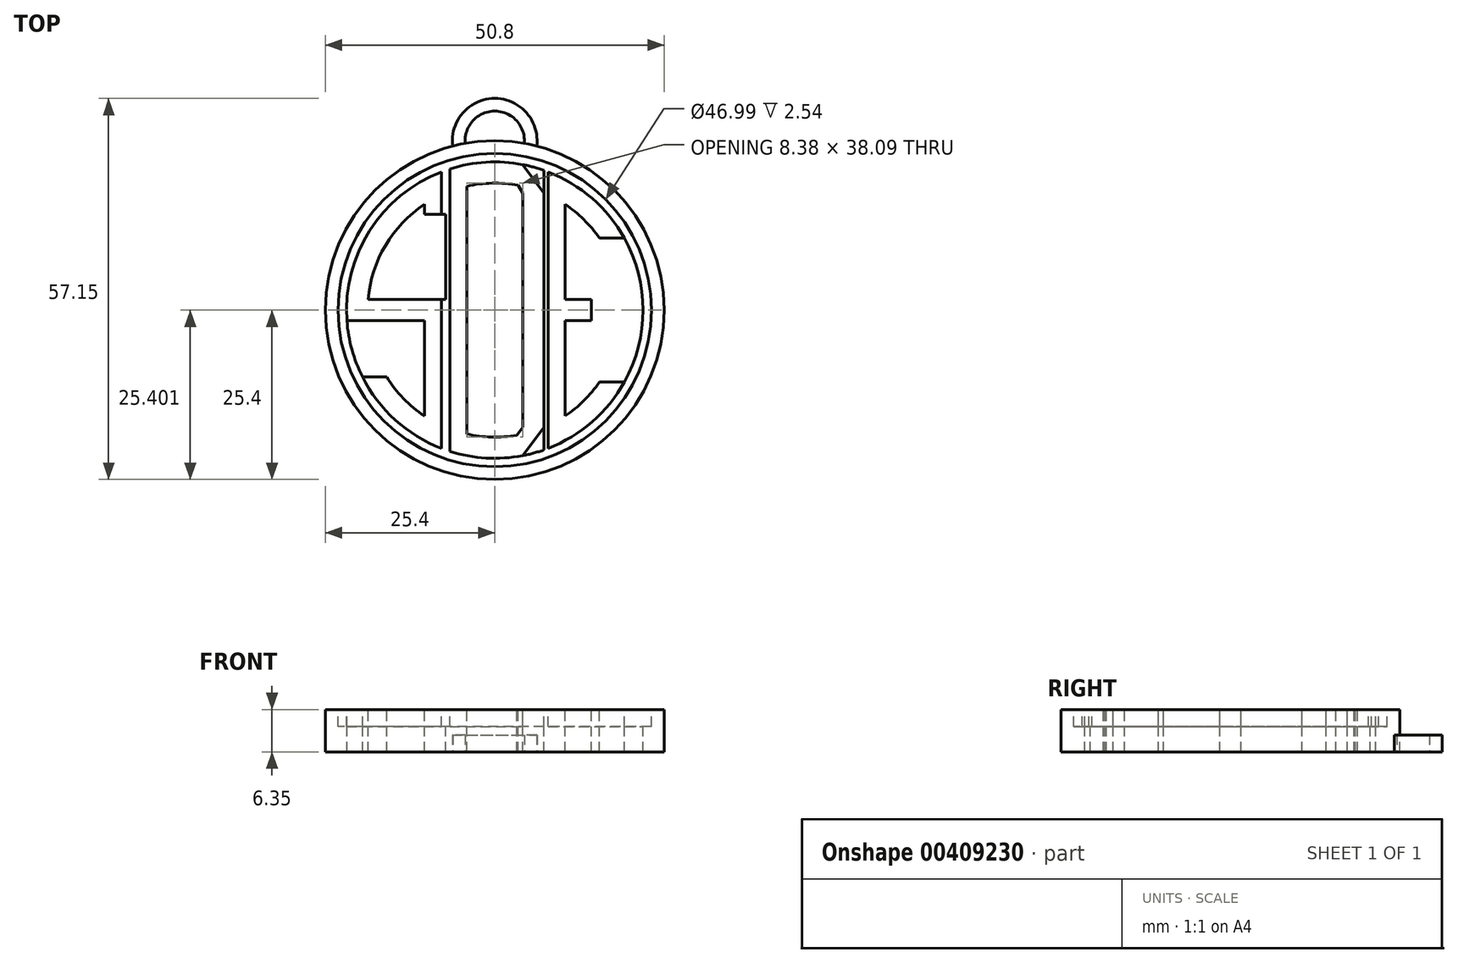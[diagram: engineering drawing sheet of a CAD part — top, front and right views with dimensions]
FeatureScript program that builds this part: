
annotation { "Feature Type Name" : "Feature", "Feature Type Description" : "" }
export const myFeature = defineFeature(function(context is Context, id is Id, definition is map)
    precondition{}
    {
        {
            var Q0;
            Q0=qCreatedBy(makeId("Top.planeOp"),FACE);
            var sketch = newSketch(context, id + "F0", { "sketchPlane" : qUnion([Q0])});
            skCircle(sketch, "E0", {"center": v(0, 0) * mm, "radius": 25.4 * mm});
            skCircle(sketch, "E1", {"center": v(0, 0) * mm, "radius": 22.23 * mm});
            skLineSegment(sketch, "E2", {"start": v(0, 0) * mm, "end": v(7.37, 0) * mm, "construction": true});
            skLineSegment(sketch, "E3", {"start": v(0, 0) * mm, "end": v(-7.37, 0) * mm, "construction": true});
            skLineSegment(sketch, "E4", {"start": v(7.37, 17.57) * mm, "end": v(7.37, 1.59) * mm});
            skLineSegment(sketch, "E5", {"start": v(-7.37, 20.97) * mm, "end": v(-7.37, -20.97) * mm, "construction": true});
            skPoint(sketch, "E6", {"position": v(-7.37, 1.59) * mm});
            skPoint(sketch, "E7", {"position": v(-7.37, -1.59) * mm});
            skArc(sketch, "E8", {"start": v(-16.2, -10.03) * mm, "mid": v(-13.68, -13.25) * mm, "end": v(-10.54, -15.87) * mm});
            skLineSegment(sketch, "E9", {"start": v(-7.37, 1.59) * mm, "end": v(-18.98, 1.59) * mm});
            skLineSegment(sketch, "E10", {"start": v(-10.54, -1.59) * mm, "end": v(-18.98, -1.59) * mm});
            skLineSegment(sketch, "E11", {"start": v(-7.37, 17.57) * mm, "end": v(-7.37, 14.4) * mm});
            skLineSegment(sketch, "E12", {"start": v(-7.37, 14.4) * mm, "end": v(-10.54, 14.4) * mm});
            skLineSegment(sketch, "E13", {"start": v(-10.54, 14.4) * mm, "end": v(-10.54, 15.87) * mm});
            skPoint(sketch, "E14", {"position": v(-10.54, -1.59) * mm});
            skLineSegment(sketch, "E15", {"start": v(-7.37, -1.59) * mm, "end": v(-7.37, -17.57) * mm});
            skLineSegment(sketch, "E16", {"start": v(-10.54, -1.59) * mm, "end": v(-10.54, -15.87) * mm});
            skLineSegment(sketch, "E17", {"start": v(-19.83, -10.03) * mm, "end": v(-16.2, -10.03) * mm});
            skPoint(sketch, "E18", {"position": v(-4.2, 0) * mm});
            skLineSegment(sketch, "E19", {"start": v(-4.2, 18.58) * mm, "end": v(-4.2, 1.59) * mm});
            skPoint(sketch, "E20", {"position": v(10.54, 0) * mm});
            skLineSegment(sketch, "E21", {"start": v(10.54, 15.87) * mm, "end": v(10.54, 1.59) * mm});
            skLineSegment(sketch, "E22", {"start": v(-18.98, -1.59) * mm, "end": v(-22.17, -1.59) * mm});
            skArc(sketch, "E23.trimOffspring", {"start": v(-10.54, 15.87) * mm, "mid": v(-16.4, 9.7) * mm, "end": v(-18.98, 1.59) * mm});
            skArc(sketch, "E24.trimOffspring", {"start": v(3.47, 18.73) * mm, "mid": v(-0.37, 19.05) * mm, "end": v(-4.2, 18.58) * mm});
            skPoint(sketch, "E25.orphan", {"position": v(7.37, 20.97) * mm});
            skLineSegment(sketch, "E26.trimOffspring", {"start": v(-4.2, -1.59) * mm, "end": v(-4.2, -18.58) * mm});
            skLineSegment(sketch, "E27.trimOffspring", {"start": v(7.37, -1.59) * mm, "end": v(7.37, -17.57) * mm});
            skArc(sketch, "E28.trimOffspring", {"start": v(-4.2, -18.58) * mm, "mid": v(-0.45, -19.04) * mm, "end": v(3.3, -18.76) * mm});
            skArc(sketch, "E29.trimOffspring", {"start": v(10.54, -15.87) * mm, "mid": v(13.36, -13.58) * mm, "end": v(15.7, -10.79) * mm});
            skLineSegment(sketch, "E30", {"start": v(-7.37, 14.4) * mm, "end": v(-7.37, 1.59) * mm});
            skPoint(sketch, "E31", {"position": v(-8, 14.4) * mm});
            skPoint(sketch, "E32", {"position": v(-6.73, 14.4) * mm});
            skLineSegment(sketch, "E33", {"start": v(-6.73, 14.4) * mm, "end": v(-8, 14.4) * mm});
            skLineSegment(sketch, "E34", {"start": v(-8, 20.73) * mm, "end": v(-8, 14.4) * mm});
            skLineSegment(sketch, "E35", {"start": v(-6.73, 14.4) * mm, "end": v(-6.73, 21.18) * mm});
            skPoint(sketch, "E36", {"position": v(4.2, 17.57) * mm});
            skLineSegment(sketch, "E37", {"start": v(4.2, 17.57) * mm, "end": v(4.2, -17.57) * mm});
            skLineSegment(sketch, "E38", {"start": v(7.37, 17.57) * mm, "end": v(7.37, 20.97) * mm});
            skLineSegment(sketch, "E39", {"start": v(-4.2, 1.59) * mm, "end": v(-4.2, -1.59) * mm});
            skLineSegment(sketch, "E40", {"start": v(14.48, 1.59) * mm, "end": v(14.48, -1.59) * mm});
            skLineSegment(sketch, "E41", {"start": v(14.48, -1.59) * mm, "end": v(10.54, -1.59) * mm});
            skLineSegment(sketch, "E42", {"start": v(15.7, 10.79) * mm, "end": v(19.43, 10.79) * mm});
            skLineSegment(sketch, "E43", {"start": v(15.7, -10.79) * mm, "end": v(19.43, -10.79) * mm});
            skPoint(sketch, "E44", {"position": v(-8, -1.59) * mm});
            skPoint(sketch, "E45", {"position": v(-6.73, -1.59) * mm});
            skLineSegment(sketch, "E46", {"start": v(-6.73, -1.59) * mm, "end": v(-8, -1.59) * mm});
            skLineSegment(sketch, "E47", {"start": v(-8, -1.59) * mm, "end": v(-8, -20.73) * mm});
            skLineSegment(sketch, "E48", {"start": v(-6.73, -1.59) * mm, "end": v(-6.73, -21.18) * mm});
            skLineSegment(sketch, "E49", {"start": v(-8, -1.59) * mm, "end": v(-8, 1.59) * mm});
            skPoint(sketch, "E50", {"position": v(-6.73, 1.56) * mm});
            skLineSegment(sketch, "E51", {"start": v(-7.37, 1.59) * mm, "end": v(-6.73, 1.56) * mm});
            skLineSegment(sketch, "E52", {"start": v(-6.73, -1.59) * mm, "end": v(-6.73, 1.56) * mm});
            skPoint(sketch, "E53", {"position": v(8, 20.97) * mm});
            skPoint(sketch, "E54", {"position": v(7.37, -20.97) * mm});
            skPoint(sketch, "E55", {"position": v(8, -20.97) * mm});
            skLineSegment(sketch, "E56", {"start": v(7.37, -20.97) * mm, "end": v(7.37, -17.57) * mm});
            skLineSegment(sketch, "E57", {"start": v(7.37, 1.59) * mm, "end": v(7.37, -1.59) * mm});
            skLineSegment(sketch, "E58", {"start": v(7.37, 17.57) * mm, "end": v(4.2, 21.83) * mm});
            skLineSegment(sketch, "E59", {"start": v(4.2, 17.57) * mm, "end": v(3.47, 18.73) * mm});
            skPoint(sketch, "E59.endSnap0", {"position": v(5.78, 19.7) * mm});
            skPoint(sketch, "E60", {"position": v(4.2, -17.57) * mm});
            skLineSegment(sketch, "E61", {"start": v(7.37, -17.57) * mm, "end": v(4.2, -21.83) * mm});
            skLineSegment(sketch, "E62", {"start": v(4.2, -17.57) * mm, "end": v(3.3, -18.76) * mm});
            skLineSegment(sketch, "E63", {"start": v(-6.73, 14.4) * mm, "end": v(-6.73, 1.56) * mm});
            skPoint(sketch, "E64.orphan", {"position": v(2.87, 19.7) * mm});
            skPoint(sketch, "E65.start.orphan", {"position": v(4.2, 18.58) * mm});
            skPoint(sketch, "E66.orphan", {"position": v(4.2, -18.58) * mm});
            skLineSegment(sketch, "E67", {"start": v(14.48, 1.59) * mm, "end": v(10.54, 1.59) * mm});
            skLineSegment(sketch, "E68.trimOffspring", {"start": v(10.54, -1.59) * mm, "end": v(10.54, -15.87) * mm});
            skArc(sketch, "E69.trimOffspring", {"start": v(15.7, 10.79) * mm, "mid": v(13.36, 13.58) * mm, "end": v(10.54, 15.87) * mm});
            skCircle(sketch, "E70", {"center": v(0, 0) * mm, "radius": 23.5 * mm});
            skLineSegment(sketch, "E71", {"start": v(8, 20.73) * mm, "end": v(8, -20.73) * mm});
            skPoint(sketch, "E72", {"position": v(8, 20.72) * mm});
            skSolve(sketch);
        }
        {
            var Q0;
            Q0=makeQuery(id+"F0.imprint","IMPRINT",FACE,{"disambiguationData":[TD([[makeQuery(id+"F0.imprint","IMPRINT",EDGE,{"derivedFrom":sQuery(id+"F0.wireOp",EDGE,"E0")}),1.0]])]});
            var Q1;
            Q1=makeQuery(id+"F0.imprint","IMPRINT",FACE,{"disambiguationData":[TD([[makeQuery(id+"F0.imprint","IMPRINT",EDGE,{"derivedFrom":sQuery(id+"F0.wireOp",EDGE,"E8")}),-1.0]])]});
            var Q2;
            {var subQ0=sQuery(id+"F0.wireOp",EDGE,"E30");Q2=makeQuery(id+"F0.imprint","IMPRINT",FACE,{"disambiguationData":[TD([[makeQuery(id+"F0.imprint","IMPRINT",EDGE,{"derivedFrom":subQ0}),1.0]])]});}
            var Q3;
            {var subQ0=sQuery(id+"F0.wireOp",EDGE,"E34");Q3=makeQuery(id+"F0.imprint","IMPRINT",FACE,{"disambiguationData":[TD([[makeQuery(id+"F0.imprint","IMPRINT",EDGE,{"derivedFrom":subQ0}),1.0]])]});}
            var Q4;
            {var subQ0=sQuery(id+"F0.wireOp",EDGE,"E49");Q4=makeQuery(id+"F0.imprint","IMPRINT",FACE,{"disambiguationData":[TD([[makeQuery(id+"F0.imprint","IMPRINT",EDGE,{"derivedFrom":subQ0}),-1.0]])]});}
            var Q5;
            Q5=makeQuery(id+"F0.imprint","IMPRINT",FACE,{"disambiguationData":[TD([[makeQuery(id+"F0.imprint","IMPRINT",EDGE,{"derivedFrom":sQuery(id+"F0.wireOp",EDGE,"E4")}),-1.0]])]});
            var Q6;
            {var subQ0=sQuery(id+"F0.wireOp",EDGE,"E47");Q6=makeQuery(id+"F0.imprint","IMPRINT",FACE,{"disambiguationData":[TD([[makeQuery(id+"F0.imprint","IMPRINT",EDGE,{"derivedFrom":subQ0}),1.0]])]});}
            var Q7;
            Q7=makeQuery(id+"F0.imprint","IMPRINT",FACE,{"disambiguationData":[TD([[makeQuery(id+"F0.imprint","IMPRINT",EDGE,{"derivedFrom":sQuery(id+"F0.wireOp",EDGE,"E21")}),-1.0]])]});
            var Q8;
            Q8=makeQuery(id+"F0.imprint","IMPRINT",FACE,{"disambiguationData":[TD([[makeQuery(id+"F0.imprint","IMPRINT",EDGE,{"derivedFrom":sQuery(id+"F0.wireOp",EDGE,"E4")}),1.0]])]});
            var Q9;
            Q9=makeQuery(id+"F0.imprint","IMPRINT",FACE,{"disambiguationData":[TD([[makeQuery(id+"F0.imprint","IMPRINT",EDGE,{"derivedFrom":sQuery(id+"F0.wireOp",EDGE,"E70")}),1.0]])]});
            extrude(context, id + "F1", {"entities" : qUnion([Q0, Q1, Q2, Q3, Q4, Q5, Q6, Q7, Q8, Q9]), "oppositeDirection" : true, "depth" : 6.35 * mm});
        }
        {
            var Q0;
            Q0=makeQuery(id+"F0.imprint","IMPRINT",FACE,{"disambiguationData":[TD([[makeQuery(id+"F0.imprint","IMPRINT",EDGE,{"derivedFrom":sQuery(id+"F0.wireOp",EDGE,"E70")}),1.0]])]});
            var Q1;
            {var subQ0=sQuery(id+"F0.wireOp",EDGE,"E34");Q1=makeQuery(id+"F0.imprint","IMPRINT",FACE,{"disambiguationData":[TD([[makeQuery(id+"F0.imprint","IMPRINT",EDGE,{"derivedFrom":subQ0}),1.0]])]});}
            var Q2;
            {var subQ0=sQuery(id+"F0.wireOp",EDGE,"E30");Q2=makeQuery(id+"F0.imprint","IMPRINT",FACE,{"disambiguationData":[TD([[makeQuery(id+"F0.imprint","IMPRINT",EDGE,{"derivedFrom":subQ0}),1.0]])]});}
            var Q3;
            {var subQ0=sQuery(id+"F0.wireOp",EDGE,"E49");Q3=makeQuery(id+"F0.imprint","IMPRINT",FACE,{"disambiguationData":[TD([[makeQuery(id+"F0.imprint","IMPRINT",EDGE,{"derivedFrom":subQ0}),-1.0]])]});}
            var Q4;
            {var subQ0=sQuery(id+"F0.wireOp",EDGE,"E47");Q4=makeQuery(id+"F0.imprint","IMPRINT",FACE,{"disambiguationData":[TD([[makeQuery(id+"F0.imprint","IMPRINT",EDGE,{"derivedFrom":subQ0}),1.0]])]});}
            var Q5;
            Q5=makeQuery(id+"F0.imprint","IMPRINT",FACE,{"disambiguationData":[TD([[makeQuery(id+"F0.imprint","IMPRINT",EDGE,{"derivedFrom":sQuery(id+"F0.wireOp",EDGE,"E4")}),1.0]])]});
            extrude(context, id + "F2", {"entities" : qUnion([Q0, Q1, Q2, Q3, Q4, Q5]), "operationType" : NewBodyOperationType.REMOVE, "oppositeDirection" : true, "depth" : 2.54 * mm});
        }
        {
            var Q0;
            Q0=makeQuery(id+"F1.opExtrude","CAP_FACE",FACE,{"disambiguationData":[OSD([sQuery(id+"F0.wireOp",EDGE,"E0"),sQuery(id+"F0.wireOp",EDGE,"E1"),sQuery(id+"F0.wireOp",EDGE,"E8"),sQuery(id+"F0.wireOp",EDGE,"E9"),sQuery(id+"F0.wireOp",EDGE,"E10"),sQuery(id+"F0.wireOp",EDGE,"E12"),sQuery(id+"F0.wireOp",EDGE,"E13"),sQuery(id+"F0.wireOp",EDGE,"E16"),sQuery(id+"F0.wireOp",EDGE,"E17"),sQuery(id+"F0.wireOp",EDGE,"E19"),sQuery(id+"F0.wireOp",EDGE,"E21"),sQuery(id+"F0.wireOp",EDGE,"E22"),sQuery(id+"F0.wireOp",EDGE,"E23.trimOffspring"),sQuery(id+"F0.wireOp",EDGE,"E24.trimOffspring"),sQuery(id+"F0.wireOp",EDGE,"E26.trimOffspring"),sQuery(id+"F0.wireOp",EDGE,"E28.trimOffspring"),sQuery(id+"F0.wireOp",EDGE,"E29.trimOffspring"),sQuery(id+"F0.wireOp",EDGE,"E30"),sQuery(id+"F0.wireOp",EDGE,"E33"),sQuery(id+"F0.wireOp",EDGE,"E37"),sQuery(id+"F0.wireOp",EDGE,"E38"),sQuery(id+"F0.wireOp",EDGE,"E39"),sQuery(id+"F0.wireOp",EDGE,"E40"),sQuery(id+"F0.wireOp",EDGE,"E41"),sQuery(id+"F0.wireOp",EDGE,"E42"),sQuery(id+"F0.wireOp",EDGE,"E43"),sQuery(id+"F0.wireOp",EDGE,"E56"),sQuery(id+"F0.wireOp",EDGE,"E58"),sQuery(id+"F0.wireOp",EDGE,"E59"),sQuery(id+"F0.wireOp",EDGE,"E61"),sQuery(id+"F0.wireOp",EDGE,"E62"),sQuery(id+"F0.wireOp",EDGE,"E67"),sQuery(id+"F0.wireOp",EDGE,"E68.trimOffspring"),sQuery(id+"F0.wireOp",EDGE,"E69.trimOffspring")])],"isStart":false});
            var sketch = newSketch(context, id + "F3", { "sketchPlane" : qUnion([Q0])});
            skPoint(sketch, "E73", {"position": v(0, -25.4) * mm});
            skArc(sketch, "E74", {"start": v(-6.3, -24.6) * mm, "mid": v(0, -31.75) * mm, "end": v(6.3, -24.6) * mm});
            skArc(sketch, "E75", {"start": v(-4.43, -25.01) * mm, "mid": v(0, -29.85) * mm, "end": v(4.43, -25.01) * mm});
            skCircle(sketch, "E76", {"center": v(0, 0) * mm, "radius": 25.4 * mm});
            skSolve(sketch);
        }
        {
            var Q0;
            {var subQ0=sQuery(id+"F3.wireOp",EDGE,"E74");Q0=makeQuery(id+"F3.imprint","IMPRINT",FACE,{"disambiguationData":[TD([[makeQuery(id+"F3.imprint","IMPRINT",EDGE,{"derivedFrom":subQ0}),1.0]])]});}
            extrude(context, id + "F4", {"entities" : qUnion([Q0]), "operationType" : NewBodyOperationType.ADD, "oppositeDirection" : true, "depth" : 2.54 * mm});
        }
    });
